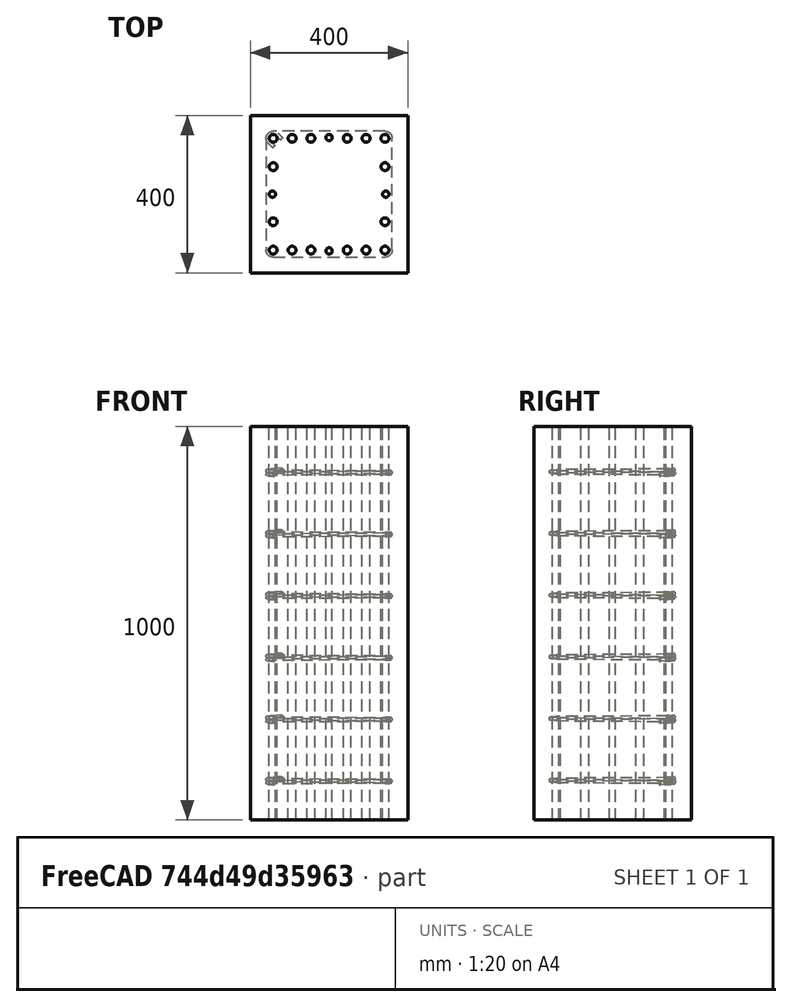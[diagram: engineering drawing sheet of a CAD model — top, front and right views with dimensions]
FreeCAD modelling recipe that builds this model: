
FCSTD DOCUMENT  (FreeCAD 0.21R33771 (Git))
Label: Column Reinforcemnent
License: All rights reserved
LicenseURL: https://en.wikipedia.org/wiki/All_rights_reserved
objects: Part::FeaturePython×16, Sketcher::SketchObject×14, App::DocumentObjectGroupPython×6, Part::Part2DObjectPython×2
note: 32 computed .brp shape members not serialized (recipe doc carries the construction recipe); baked Part::Feature solids carry a one-line shape summary decoded from their .brp

FEATURE [Part::Part2DObjectPython] Rectangle  # Draft 2D object (typed FeaturePython)
  Area = 160000
  ChamferSize = 0
  Columns = 1
  FilletRadius = 0
  Height = 400
  Length = 400
  MakeFace = true
  Rows = 1
FEATURE [Part::FeaturePython] Structure  # Arch/BIM 13 (typed FeaturePython)
  Base = -> Rectangle
  BaseMirror = false
  BaseOffsetX = 0
  BaseOffsetY = 0
  BasePerpendicularToTool = false
  BaseRotation = 0
  ComputedLength = 1000
  FaceMaker = 0
  Height = 1000
  HorizontalArea = 160000
  IfcData = attributes={"GlobalId": {"name": "GlobalId", "type": "IfcGloballyUniqueId", "is_enum": false, "enum_values": []}, "Description": {"... (+484 chars omitted),+1 more (map truncated)
  IfcType = 13
  Length = 0
  MoveBase = false
  MoveWithHost = false
  Nodes = (2) [(200,200,0),(200,200,1000)]
  NodesOffset = 0
  Normal = (0,0,0)
  PerimeterLength = 1600
  PredefinedType = 0
  ToolOffsetFirst = 0
  ToolOffsetLast = 0
  VerticalArea = 1600000
  Width = 100
FEATURE [Sketcher::SketchObject] Sketch
  FullyConstrained = false
  MapMode = 5
  Placement = pos=(0,400,0) rot=(0,0.707107,0.707107;3.14159rad)
  Support = -> [Structure]
  sketch-geometry (1):
    g0: LineSegment StartX=-58 StartY=0 StartZ=0 EndX=-58 EndY=1000 EndZ=0
FEATURE [Part::FeaturePython] Rebar  label="StraightRebar"  # Arch/BIM 110 (typed FeaturePython)
  Amount = 2
  AmountCheck = true
  Base = -> Sketch
  Cover = 48
  CoverAlong = Right Side
  Diameter = 20
  Direction = (0,0,0)
  Distance = 0
  FrontCover = 48
  HorizontalArea = 0
  Host = -> Structure
  IfcType = 110
  LeftBottomCover = 0
  Length = 1000
  Mark = StraightRebar
  MoveBase = false
  MoveWithHost = false
  OffsetEnd = 58
  OffsetStart = 58
  Orientation = Vertical
  PerimeterLength = 0
  PlacementList = 2 placements: [(0,-58,1.28786e-14),(0,-342,7.59393e-14)]
  RebarShape = 0
  RightTopCover = 0
  Rounding = 0
  Spacing = 284
  TotalLength = 2000
  TrueSpacing = 2
  VerticalArea = 0
FEATURE [Sketcher::SketchObject] Sketch001
  FullyConstrained = false
  MapMode = 5
  Placement = pos=(0,400,0) rot=(0,0.707107,0.707107;3.14159rad)
  Support = -> [Structure]
  sketch-geometry (1):
    g0: LineSegment StartX=-342 StartY=0 StartZ=0 EndX=-342 EndY=1000 EndZ=0
FEATURE [Part::FeaturePython] Rebar001  label="StraightRebar001"  # Arch/BIM 110 (typed FeaturePython)
  Amount = 2
  AmountCheck = true
  Base = -> Sketch001
  Cover = 48
  CoverAlong = Left Side
  Diameter = 20
  Direction = (0,0,0)
  Distance = 0
  FrontCover = 48
  HorizontalArea = 0
  Host = -> Structure
  IfcType = 110
  LeftBottomCover = 0
  Length = 1000
  Mark = StraightRebar001
  MoveBase = false
  MoveWithHost = false
  OffsetEnd = 58
  OffsetStart = 58
  Orientation = Vertical
  PerimeterLength = 0
  PlacementList = 2 placements: [(0,-58,1.28786e-14),(0,-342,7.59393e-14)]
  RebarShape = 0
  RightTopCover = 0
  Rounding = 0
  Spacing = 284
  TotalLength = 2000
  TrueSpacing = 2
  VerticalArea = 0
FEATURE [Part::Part2DObjectPython] Wire  # Draft 2D object (typed FeaturePython)
  Area = 0
  ChamferSize = 0
  Closed = false
  End = (59.4142,320.787,-10.6346)
  FilletRadius = 0
  Length = 1387.31
  MakeFace = true
  Points = (7) [(79.2132,340.586,2.12692),(44,375.799,0),(44,44,-2.12692),(356,44,-4.25383),(356,356,-6.38075),(24.201,356,-8.50767),(59.4142,320.787,-10.6346)]
  Start = (79.2132,340.586,2.12692)
  Subdivisions = 0
  Support = -> [Structure]
FEATURE [Part::FeaturePython] Rebar002  label="Stirrup"  # Arch/BIM 110 (typed FeaturePython)
  Amount = 6
  AmountCheck = true
  Base = -> Wire
  BentAngle = 135
  BentFactor = 2
  BottomCover = 40
  Diameter = 8
  Direction = (0,0,1)
  Distance = 0
  FrontCover = 100
  HorizontalArea = 0
  Host = -> Structure
  IfcType = 110
  LeftCover = 40
  Length = 1387.31
  Mark = Stirrup
  MoveBase = false
  MoveWithHost = false
  OffsetEnd = 104
  OffsetStart = 104
  PerimeterLength = 0
  PlacementList = 6 placements: arithmetic series from (0,0,104) step (0,0,156.8) to (0,0,888)
  RebarShape = 3
  RightCover = 40
  Rounding = 1.75
  Spacing = 156.8
  TopCover = 40
  TotalLength = 8323.89
  TrueSpacing = 6
  VerticalArea = 0
FEATURE [App::DocumentObjectGroupPython] Ties  # scripted group (container) (typed FeaturePython)
  BottomCover = 40
  Group = -> [Rebar002]
  LeftCover = 40
  RightCover = 40
  Ties = -> [Rebar002]
  TiesConfiguration = SingleTie
  TopCover = 40
FEATURE [App::DocumentObjectGroupPython] MainRebars  # scripted group (container) (typed FeaturePython)
  BottomOffset = 0
  Group = -> [Rebar,Rebar001]
  HookExtendAlong = x-axis
  HookExtension = 40
  HookOrientation = Top Inside
  MainRebars = -> [Rebar,Rebar001]
  RebarType = StraightRebar
  TopOffset = 0
FEATURE [Sketcher::SketchObject] Sketch002
  FullyConstrained = false
  MapMode = 5
  Placement = pos=(0,0,0) rot=(0.57735,-0.57735,-0.57735;2.0944rad)
  Support = -> [Structure]
  sketch-geometry (1):
    g0: LineSegment StartX=-58 StartY=0 StartZ=0 EndX=-58 EndY=1000 EndZ=0
FEATURE [Part::FeaturePython] Rebar003  label="StraightRebar002"  # Arch/BIM 110 (typed FeaturePython)
  Amount = 2
  AmountCheck = true
  Base = -> Sketch002
  Cover = 48
  CoverAlong = Right Side
  Diameter = 20
  Direction = (0,0,0)
  Distance = 0
  FrontCover = 96
  HorizontalArea = 0
  Host = -> Structure
  IfcType = 110
  LeftBottomCover = 0
  Length = 1000
  Mark = StraightRebar002
  MoveBase = false
  MoveWithHost = false
  OffsetEnd = 246
  OffsetStart = 106
  Orientation = Vertical
  PerimeterLength = 0
  PlacementList = 2 placements: [(106,0,0),(154,0,0)]
  RebarShape = 0
  RightTopCover = 0
  Rounding = 0
  Spacing = 48
  TotalLength = 2000
  TrueSpacing = 2
  VerticalArea = 0
FEATURE [Sketcher::SketchObject] Sketch003
  FullyConstrained = false
  MapMode = 5
  Placement = pos=(0,0,0) rot=(0.57735,-0.57735,-0.57735;2.0944rad)
  Support = -> [Structure]
  sketch-geometry (1):
    g0: LineSegment StartX=-56 StartY=0 StartZ=0 EndX=-56 EndY=1000 EndZ=0
FEATURE [Part::FeaturePython] Rebar004  label="StraightRebar003"  # Arch/BIM 110 (typed FeaturePython)
  Amount = 1
  AmountCheck = true
  Base = -> Sketch003
  Cover = 48
  CoverAlong = Right Side
  Diameter = 16
  Direction = (0,0,0)
  Distance = 0
  FrontCover = 192
  HorizontalArea = 0
  Host = -> Structure
  IfcType = 110
  LeftBottomCover = 0
  Length = 1000
  Mark = StraightRebar003
  MoveBase = false
  MoveWithHost = false
  OffsetEnd = 200
  OffsetStart = 200
  Orientation = Vertical
  PerimeterLength = 0
  PlacementList = 1 placements: [(200,0,0)]
  RebarShape = 0
  RightTopCover = 0
  Rounding = 0
  Spacing = 0
  TotalLength = 1000
  TrueSpacing = 1
  VerticalArea = 0
FEATURE [Sketcher::SketchObject] Sketch004
  FullyConstrained = false
  MapMode = 5
  Placement = pos=(0,0,0) rot=(0.57735,-0.57735,-0.57735;2.0944rad)
  Support = -> [Structure]
  sketch-geometry (1):
    g0: LineSegment StartX=-58 StartY=0 StartZ=0 EndX=-58 EndY=1000 EndZ=0
FEATURE [Part::FeaturePython] Rebar005  label="StraightRebar004"  # Arch/BIM 110 (typed FeaturePython)
  Amount = 2
  AmountCheck = true
  Base = -> Sketch004
  Cover = 48
  CoverAlong = Right Side
  Diameter = 20
  Direction = (0,0,0)
  Distance = 0
  FrontCover = 236
  HorizontalArea = 0
  Host = -> Structure
  IfcType = 110
  LeftBottomCover = 0
  Length = 1000
  Mark = StraightRebar004
  MoveBase = false
  MoveWithHost = false
  OffsetEnd = 106
  OffsetStart = 246
  Orientation = Vertical
  PerimeterLength = 0
  PlacementList = 2 placements: [(246,0,0),(294,0,0)]
  RebarShape = 0
  RightTopCover = 0
  Rounding = 0
  Spacing = 48
  TotalLength = 2000
  TrueSpacing = 2
  VerticalArea = 0
FEATURE [Sketcher::SketchObject] Sketch005
  FullyConstrained = false
  MapMode = 5
  Placement = pos=(0,0,0) rot=(0.57735,-0.57735,-0.57735;2.0944rad)
  Support = -> [Structure]
  sketch-geometry (1):
    g0: LineSegment StartX=-342 StartY=0 StartZ=0 EndX=-342 EndY=1000 EndZ=0
FEATURE [Part::FeaturePython] Rebar006  label="StraightRebar005"  # Arch/BIM 110 (typed FeaturePython)
  Amount = 2
  AmountCheck = true
  Base = -> Sketch005
  Cover = 48
  CoverAlong = Left Side
  Diameter = 20
  Direction = (0,0,0)
  Distance = 0
  FrontCover = 96
  HorizontalArea = 0
  Host = -> Structure
  IfcType = 110
  LeftBottomCover = 0
  Length = 1000
  Mark = StraightRebar005
  MoveBase = false
  MoveWithHost = false
  OffsetEnd = 246
  OffsetStart = 106
  Orientation = Vertical
  PerimeterLength = 0
  PlacementList = 2 placements: [(106,0,0),(154,0,0)]
  RebarShape = 0
  RightTopCover = 0
  Rounding = 0
  Spacing = 48
  TotalLength = 2000
  TrueSpacing = 2
  VerticalArea = 0
FEATURE [Sketcher::SketchObject] Sketch006
  FullyConstrained = false
  MapMode = 5
  Placement = pos=(0,0,0) rot=(0.57735,-0.57735,-0.57735;2.0944rad)
  Support = -> [Structure]
  sketch-geometry (1):
    g0: LineSegment StartX=-344 StartY=0 StartZ=0 EndX=-344 EndY=1000 EndZ=0
FEATURE [Part::FeaturePython] Rebar007  label="StraightRebar006"  # Arch/BIM 110 (typed FeaturePython)
  Amount = 1
  AmountCheck = true
  Base = -> Sketch006
  Cover = 48
  CoverAlong = Left Side
  Diameter = 16
  Direction = (0,0,0)
  Distance = 0
  FrontCover = 192
  HorizontalArea = 0
  Host = -> Structure
  IfcType = 110
  LeftBottomCover = 0
  Length = 1000
  Mark = StraightRebar006
  MoveBase = false
  MoveWithHost = false
  OffsetEnd = 200
  OffsetStart = 200
  Orientation = Vertical
  PerimeterLength = 0
  PlacementList = 1 placements: [(200,0,0)]
  RebarShape = 0
  RightTopCover = 0
  Rounding = 0
  Spacing = 0
  TotalLength = 1000
  TrueSpacing = 1
  VerticalArea = 0
FEATURE [Sketcher::SketchObject] Sketch007
  FullyConstrained = false
  MapMode = 5
  Placement = pos=(0,0,0) rot=(0.57735,-0.57735,-0.57735;2.0944rad)
  Support = -> [Structure]
  sketch-geometry (1):
    g0: LineSegment StartX=-342 StartY=0 StartZ=0 EndX=-342 EndY=1000 EndZ=0
FEATURE [Part::FeaturePython] Rebar008  label="StraightRebar007"  # Arch/BIM 110 (typed FeaturePython)
  Amount = 2
  AmountCheck = true
  Base = -> Sketch007
  Cover = 48
  CoverAlong = Left Side
  Diameter = 20
  Direction = (0,0,0)
  Distance = 0
  FrontCover = 236
  HorizontalArea = 0
  Host = -> Structure
  IfcType = 110
  LeftBottomCover = 0
  Length = 1000
  Mark = StraightRebar007
  MoveBase = false
  MoveWithHost = false
  OffsetEnd = 106
  OffsetStart = 246
  Orientation = Vertical
  PerimeterLength = 0
  PlacementList = 2 placements: [(246,0,0),(294,0,0)]
  RebarShape = 0
  RightTopCover = 0
  Rounding = 0
  Spacing = 48
  TotalLength = 2000
  TrueSpacing = 2
  VerticalArea = 0
FEATURE [Sketcher::SketchObject] Sketch008
  FullyConstrained = false
  MapMode = 5
  Placement = pos=(0,400,0) rot=(0,0.707107,0.707107;3.14159rad)
  Support = -> [Structure]
  sketch-geometry (1):
    g0: LineSegment StartX=-58 StartY=0 StartZ=0 EndX=-58 EndY=1000 EndZ=0
FEATURE [Part::FeaturePython] Rebar009  label="StraightRebar008"  # Arch/BIM 110 (typed FeaturePython)
  Amount = 1
  AmountCheck = true
  Base = -> Sketch008
  Cover = 48
  CoverAlong = Right Side
  Diameter = 20
  Direction = (0,0,0)
  Distance = 0
  FrontCover = 120
  HorizontalArea = 0
  Host = -> Structure
  IfcType = 110
  LeftBottomCover = 0
  Length = 1000
  Mark = StraightRebar008
  MoveBase = false
  MoveWithHost = false
  OffsetEnd = 270
  OffsetStart = 130
  Orientation = Vertical
  PerimeterLength = 0
  PlacementList = 1 placements: [(0,-130,2.88658e-14)]
  RebarShape = 0
  RightTopCover = 0
  Rounding = 0
  Spacing = 0
  TotalLength = 1000
  TrueSpacing = 1
  VerticalArea = 0
FEATURE [Sketcher::SketchObject] Sketch009
  FullyConstrained = false
  MapMode = 5
  Placement = pos=(0,400,0) rot=(0,0.707107,0.707107;3.14159rad)
  Support = -> [Structure]
  sketch-geometry (1):
    g0: LineSegment StartX=-56 StartY=0 StartZ=0 EndX=-56 EndY=1000 EndZ=0
FEATURE [Part::FeaturePython] Rebar010  label="StraightRebar009"  # Arch/BIM 110 (typed FeaturePython)
  Amount = 1
  AmountCheck = true
  Base = -> Sketch009
  Cover = 48
  CoverAlong = Right Side
  Diameter = 16
  Direction = (0,0,0)
  Distance = 0
  FrontCover = 192
  HorizontalArea = 0
  Host = -> Structure
  IfcType = 110
  LeftBottomCover = 0
  Length = 1000
  Mark = StraightRebar009
  MoveBase = false
  MoveWithHost = false
  OffsetEnd = 200
  OffsetStart = 200
  Orientation = Vertical
  PerimeterLength = 0
  PlacementList = 1 placements: [(0,-200,4.44089e-14)]
  RebarShape = 0
  RightTopCover = 0
  Rounding = 0
  Spacing = 0
  TotalLength = 1000
  TrueSpacing = 1
  VerticalArea = 0
FEATURE [Sketcher::SketchObject] Sketch010
  FullyConstrained = false
  MapMode = 5
  Placement = pos=(0,400,0) rot=(0,0.707107,0.707107;3.14159rad)
  Support = -> [Structure]
  sketch-geometry (1):
    g0: LineSegment StartX=-58 StartY=0 StartZ=0 EndX=-58 EndY=1000 EndZ=0
FEATURE [Part::FeaturePython] Rebar011  label="StraightRebar010"  # Arch/BIM 110 (typed FeaturePython)
  Amount = 1
  AmountCheck = true
  Base = -> Sketch010
  Cover = 48
  CoverAlong = Right Side
  Diameter = 20
  Direction = (0,0,0)
  Distance = 0
  FrontCover = 260
  HorizontalArea = 0
  Host = -> Structure
  IfcType = 110
  LeftBottomCover = 0
  Length = 1000
  Mark = StraightRebar010
  MoveBase = false
  MoveWithHost = false
  OffsetEnd = 130
  OffsetStart = 270
  Orientation = Vertical
  PerimeterLength = 0
  PlacementList = 1 placements: [(0,-270,5.9952e-14)]
  RebarShape = 0
  RightTopCover = 0
  Rounding = 0
  Spacing = 0
  TotalLength = 1000
  TrueSpacing = 1
  VerticalArea = 0
FEATURE [Sketcher::SketchObject] Sketch011
  FullyConstrained = false
  MapMode = 5
  Placement = pos=(0,400,0) rot=(0,0.707107,0.707107;3.14159rad)
  Support = -> [Structure]
  sketch-geometry (1):
    g0: LineSegment StartX=-342 StartY=0 StartZ=0 EndX=-342 EndY=1000 EndZ=0
FEATURE [Part::FeaturePython] Rebar012  label="StraightRebar011"  # Arch/BIM 110 (typed FeaturePython)
  Amount = 1
  AmountCheck = true
  Base = -> Sketch011
  Cover = 48
  CoverAlong = Left Side
  Diameter = 20
  Direction = (0,0,0)
  Distance = 0
  FrontCover = 120
  HorizontalArea = 0
  Host = -> Structure
  IfcType = 110
  LeftBottomCover = 0
  Length = 1000
  Mark = StraightRebar011
  MoveBase = false
  MoveWithHost = false
  OffsetEnd = 270
  OffsetStart = 130
  Orientation = Vertical
  PerimeterLength = 0
  PlacementList = 1 placements: [(0,-130,2.88658e-14)]
  RebarShape = 0
  RightTopCover = 0
  Rounding = 0
  Spacing = 0
  TotalLength = 1000
  TrueSpacing = 1
  VerticalArea = 0
FEATURE [Sketcher::SketchObject] Sketch012
  FullyConstrained = false
  MapMode = 5
  Placement = pos=(0,400,0) rot=(0,0.707107,0.707107;3.14159rad)
  Support = -> [Structure]
  sketch-geometry (1):
    g0: LineSegment StartX=-344 StartY=0 StartZ=0 EndX=-344 EndY=1000 EndZ=0
FEATURE [Part::FeaturePython] Rebar013  label="StraightRebar012"  # Arch/BIM 110 (typed FeaturePython)
  Amount = 1
  AmountCheck = true
  Base = -> Sketch012
  Cover = 48
  CoverAlong = Left Side
  Diameter = 16
  Direction = (0,0,0)
  Distance = 0
  FrontCover = 192
  HorizontalArea = 0
  Host = -> Structure
  IfcType = 110
  LeftBottomCover = 0
  Length = 1000
  Mark = StraightRebar012
  MoveBase = false
  MoveWithHost = false
  OffsetEnd = 200
  OffsetStart = 200
  Orientation = Vertical
  PerimeterLength = 0
  PlacementList = 1 placements: [(0,-200,4.44089e-14)]
  RebarShape = 0
  RightTopCover = 0
  Rounding = 0
  Spacing = 0
  TotalLength = 1000
  TrueSpacing = 1
  VerticalArea = 0
FEATURE [Sketcher::SketchObject] Sketch013
  FullyConstrained = false
  MapMode = 5
  Placement = pos=(0,400,0) rot=(0,0.707107,0.707107;3.14159rad)
  Support = -> [Structure]
  sketch-geometry (1):
    g0: LineSegment StartX=-342 StartY=0 StartZ=0 EndX=-342 EndY=1000 EndZ=0
FEATURE [Part::FeaturePython] Rebar014  label="StraightRebar013"  # Arch/BIM 110 (typed FeaturePython)
  Amount = 1
  AmountCheck = true
  Base = -> Sketch013
  Cover = 48
  CoverAlong = Left Side
  Diameter = 20
  Direction = (0,0,0)
  Distance = 0
  FrontCover = 260
  HorizontalArea = 0
  Host = -> Structure
  IfcType = 110
  LeftBottomCover = 0
  Length = 1000
  Mark = StraightRebar013
  MoveBase = false
  MoveWithHost = false
  OffsetEnd = 130
  OffsetStart = 270
  Orientation = Vertical
  PerimeterLength = 0
  PlacementList = 1 placements: [(0,-270,5.9952e-14)]
  RebarShape = 0
  RightTopCover = 0
  Rounding = 0
  Spacing = 0
  TotalLength = 1000
  TrueSpacing = 1
  VerticalArea = 0
FEATURE [App::DocumentObjectGroupPython] XDirRebars  # scripted group (container) (typed FeaturePython)
  BottomOffset = 0
  Group = -> [Rebar003,Rebar004,Rebar005,Rebar006,Rebar007,Rebar008]
  HookExtension = 0
  HookOrientation = Top Inside
  NumberDiameter = 2#20mm+1#16mm+2#20mm
  RebarType = StraightRebar
  TopOffset = 0
  XDirRebars = -> [Rebar003,Rebar004,Rebar005,Rebar006,Rebar007,Rebar008]
FEATURE [App::DocumentObjectGroupPython] YDirRebars  # scripted group (container) (typed FeaturePython)
  BottomOffset = 0
  Group = -> [Rebar009,Rebar010,Rebar011,Rebar012,Rebar013,Rebar014]
  HookExtension = 0
  HookOrientation = Top Inside
  NumberDiameter = 1#20mm+1#16mm+1#20mm
  RebarType = StraightRebar
  TopOffset = 0
  YDirRebars = -> [Rebar009,Rebar010,Rebar011,Rebar012,Rebar013,Rebar014]
FEATURE [App::DocumentObjectGroupPython] SecondaryRebars  # scripted group (container) (typed FeaturePython)
  Group = -> [XDirRebars,YDirRebars]
  SecondaryRebars = -> [XDirRebars,YDirRebars]
FEATURE [App::DocumentObjectGroupPython] ColumnReinforcement  # scripted group (container) (typed FeaturePython)
  ColumnType = RectangularColumn
  Group = -> [Ties,MainRebars,SecondaryRebars]
  RebarGroups = -> [Ties,MainRebars,SecondaryRebars]
